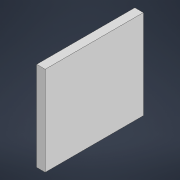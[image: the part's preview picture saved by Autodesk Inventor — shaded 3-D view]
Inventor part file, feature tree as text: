
AUTODESK INVENTOR PART (.ipt)
format: ipt  version: 2022 (Build 260153000, 153)  size: 84,992 bytes
history: native  units: mm
features: other x1, extrude x1, sketch x1
ambient origin geometry x8: Origin, YZ Plane, XZ Plane, XY Plane, X Axis, Y Axis, Z Axis, Center Point
bodies: Body1 (feature_tree)
feature tree (3):
  other  "Твердое тело1"
  extrude  "Выдавливание1"  Depth=230.0mm
  sketch  "Эскиз1"
